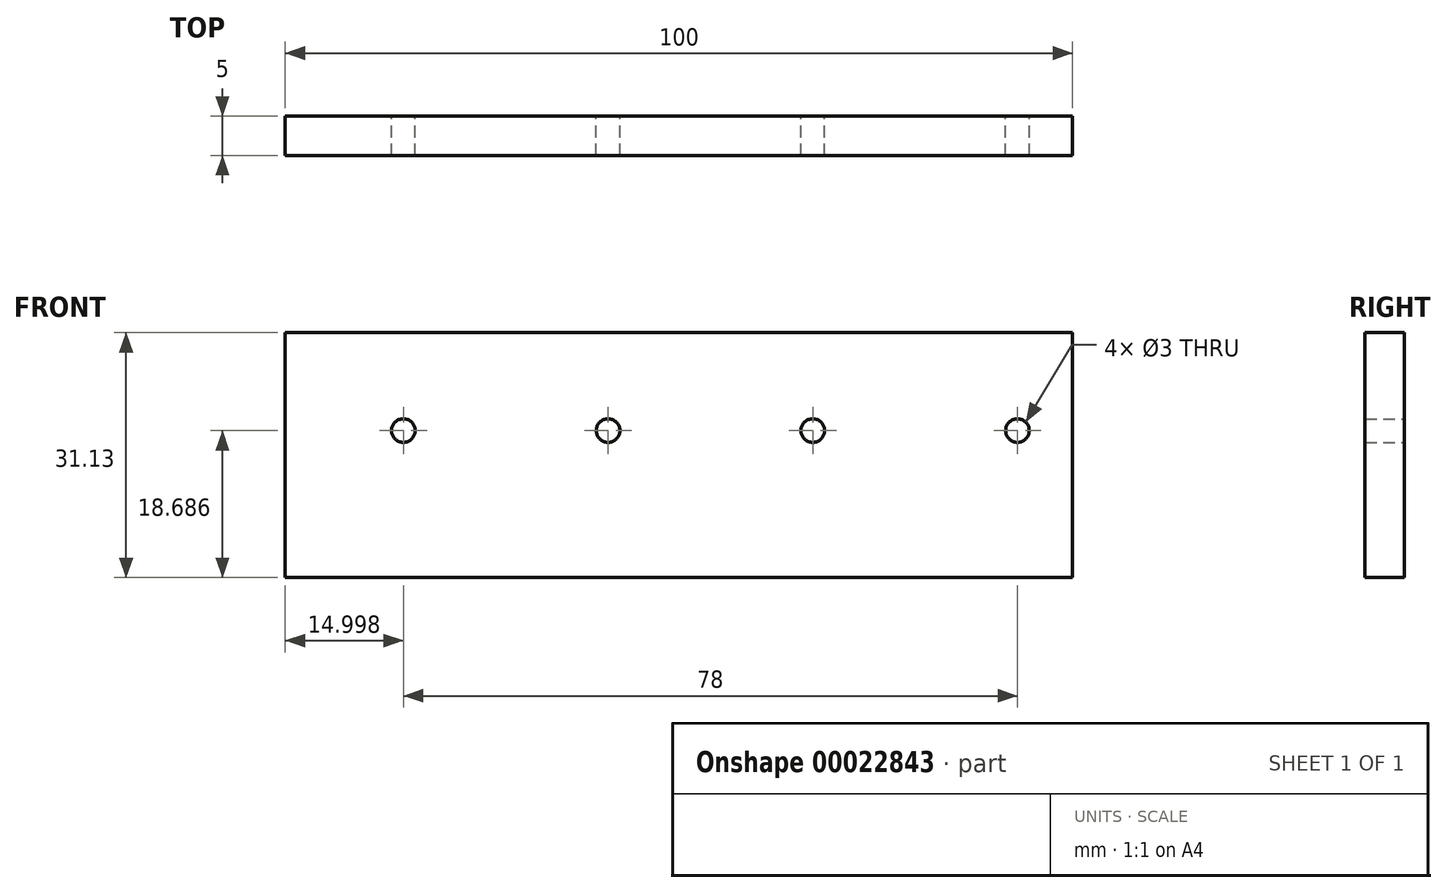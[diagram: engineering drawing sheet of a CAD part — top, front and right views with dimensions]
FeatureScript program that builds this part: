
annotation { "Feature Type Name" : "Feature", "Feature Type Description" : "" }
export const myFeature = defineFeature(function(context is Context, id is Id, definition is map)
    precondition{}
    {
        {
            var Q0;
            Q0=qCreatedBy(makeId("Front.planeOp"),FACE);
            var sketch = newSketch(context, id + "F0", { "sketchPlane" : qUnion([Q0])});
            skLineSegment(sketch, "E0.bottom", {"start": v(-86.38, 57.05) * mm, "end": v(13.62, 57.05) * mm});
            skLineSegment(sketch, "E0.top", {"start": v(-86.38, 25.92) * mm, "end": v(13.62, 25.92) * mm});
            skLineSegment(sketch, "E0.left", {"start": v(-86.38, 57.05) * mm, "end": v(-86.38, 25.92) * mm});
            skLineSegment(sketch, "E0.right", {"start": v(13.62, 57.05) * mm, "end": v(13.62, 25.92) * mm});
            skCircle(sketch, "E1", {"center": v(-71.38, 44.6) * mm, "radius": 1.5 * mm});
            skCircle(sketch, "E2", {"center": v(-45.38, 44.6) * mm, "radius": 1.5 * mm});
            skCircle(sketch, "E3", {"center": v(-19.38, 44.6) * mm, "radius": 1.5 * mm});
            skCircle(sketch, "E4", {"center": v(6.62, 44.6) * mm, "radius": 1.5 * mm});
            skSolve(sketch);
        }
        {
            var Q0;
            Q0=makeQuery(id+"F0.imprint","IMPRINT",FACE,{"disambiguationData":[TD([[makeQuery(id+"F0.imprint","IMPRINT",EDGE,{"derivedFrom":sQuery(id+"F0.wireOp",EDGE,"E0.bottom")}),-1.0]])]});
            extrude(context, id + "F1", {"entities" : qUnion([Q0]), "depth" : 5 * mm});
        }
    });
